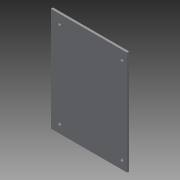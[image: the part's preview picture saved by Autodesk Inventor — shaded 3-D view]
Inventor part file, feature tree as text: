
AUTODESK INVENTOR PART (.ipt)
format: ipt  version: 2014 (Build 180170000, 170)  size: 73,728 bytes
history: native  units: mm
features: plane x1, extrude x1, sketch x1
ambient origin geometry x8: Origin, YZ Plane, XZ Plane, XY Plane, X Axis, Y Axis, Z Axis, Center Point
bodies: Body1 (feature_tree)
feature tree (3):
  plane  "Work Plane1"
  extrude  "Extrusion2"  [1 undecoded]
  sketch  "Sketch2"  dims[d5=3.0mm d6=0.0mm]
note: 1 required parameter value undecoded (feature->parameter linkage not recoverable at this tier; creation-order binding heuristic only, values carry confidence <= 0.55)
